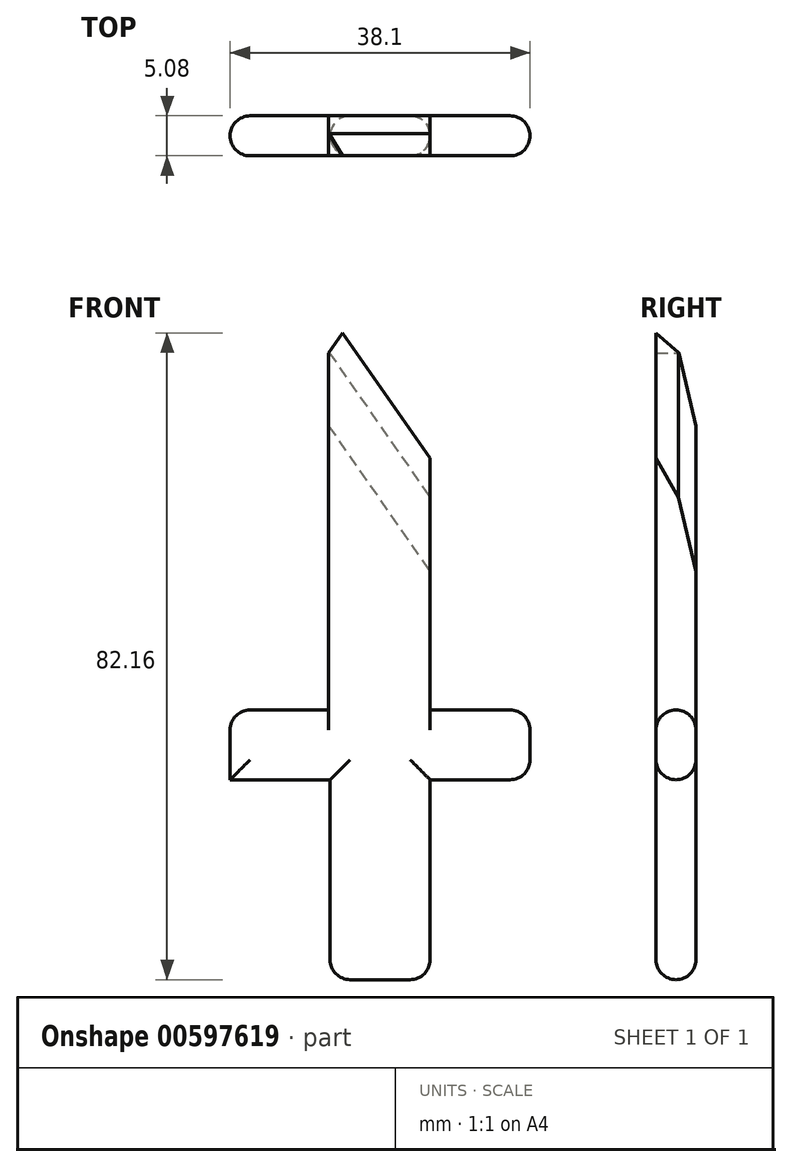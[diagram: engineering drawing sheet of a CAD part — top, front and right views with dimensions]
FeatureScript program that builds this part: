
annotation { "Feature Type Name" : "Feature", "Feature Type Description" : "" }
export const myFeature = defineFeature(function(context is Context, id is Id, definition is map)
    precondition{}
    {
        {
            var Q0;
            Q0=qCreatedBy(makeId("Front.planeOp"),FACE);
            var sketch = newSketch(context, id + "F0", { "sketchPlane" : qUnion([Q0])});
            skLineSegment(sketch, "E0.bottom", {"start": v(-30.16, 1.34) * mm, "end": v(-17.46, 1.34) * mm});
            skLineSegment(sketch, "E0.top", {"start": v(-30.16, -24.06) * mm, "end": v(-17.46, -24.06) * mm});
            skLineSegment(sketch, "E0.left", {"start": v(-30.16, 1.34) * mm, "end": v(-30.16, -24.06) * mm});
            skLineSegment(sketch, "E0.right", {"start": v(-17.46, 1.34) * mm, "end": v(-17.46, -24.06) * mm});
            skLineSegment(sketch, "E1.bottom", {"start": v(-30.16, 1.34) * mm, "end": v(-42.86, 1.34) * mm});
            skLineSegment(sketch, "E1.top", {"start": v(-30.16, 10.21) * mm, "end": v(-42.86, 10.21) * mm});
            skLineSegment(sketch, "E1.left", {"start": v(-30.16, 1.34) * mm, "end": v(-30.16, 10.21) * mm});
            skLineSegment(sketch, "E1.right", {"start": v(-42.86, 1.34) * mm, "end": v(-42.86, 10.21) * mm});
            skLineSegment(sketch, "E2.bottom", {"start": v(-17.46, 1.34) * mm, "end": v(-4.76, 1.34) * mm});
            skLineSegment(sketch, "E2.top", {"start": v(-17.46, 10.21) * mm, "end": v(-4.76, 10.21) * mm});
            skLineSegment(sketch, "E2.left", {"start": v(-17.46, 1.34) * mm, "end": v(-17.46, 10.21) * mm});
            skLineSegment(sketch, "E2.right", {"start": v(-4.76, 1.34) * mm, "end": v(-4.76, 10.21) * mm});
            skLineSegment(sketch, "E3", {"start": v(-17.46, 10.21) * mm, "end": v(-30.16, 10.21) * mm});
            skSolve(sketch);
        }
        {
            var Q0;
            Q0=qCreatedBy(makeId("Front.planeOp"),FACE);
            var sketch = newSketch(context, id + "F1", { "sketchPlane" : qUnion([Q0])});
            skLineSegment(sketch, "E4", {"start": v(-17.48, 10.21) * mm, "end": v(-17.48, 55.53) * mm});
            skLineSegment(sketch, "E5", {"start": v(-17.48, 55.53) * mm, "end": v(-23.92, 64.76) * mm});
            skLineSegment(sketch, "E6", {"start": v(-23.92, 64.76) * mm, "end": v(-30.35, 55.53) * mm});
            skLineSegment(sketch, "E7", {"start": v(-30.35, 55.53) * mm, "end": v(-30.35, 10.21) * mm});
            skLineSegment(sketch, "E8", {"start": v(-17.48, 10.21) * mm, "end": v(-30.35, 10.21) * mm});
            skSolve(sketch);
        }
        {
            var Q0;
            Q0 = qSketchRegion(id + "F0", true);
            extrude(context, id + "F2", {"entities" : qUnion([Q0]), "endBound" : BoundingType.SYMMETRIC, "depth" : 5.08 * mm, "offsetDistance" : 25.4 * mm});
        }
        {
            var Q0;
            Q0 = qSketchRegion(id + "F1", true);
            extrude(context, id + "F3", {"entities" : qUnion([Q0]), "operationType" : NewBodyOperationType.ADD, "endBound" : BoundingType.SYMMETRIC, "depth" : 5.08 * mm, "offsetDistance" : 25.4 * mm});
        }
        {
            var Q0;
            Q0=makeQuery(id+"F2.opExtrude","CAP_EDGE",EDGE,{"disambiguationData":[OSD([sQuery(id+"F0.wireOp",EDGE,"E2.bottom")])],"isStart":true});
            var Q1;
            Q1=makeQuery(id+"F2.opExtrude","CAP_EDGE",EDGE,{"disambiguationData":[OSD([sQuery(id+"F0.wireOp",EDGE,"E2.bottom")])],"isStart":false});
            var Q2;
            {var subQ0=sQuery(id+"F0.wireOp",EDGE,"E2.right");var subQ2=sQuery(id+"F0.wireOp",EDGE,"E3");var subQ3=sQuery(id+"F0.wireOp",EDGE,"E2.top");var subQ4=sQuery(id+"F0.wireOp",EDGE,"E1.top");Q2=makeQuery(id+"F3.boolean.opBoolean","SPLIT",EDGE,{"disambiguationData":[TD([makeQuery(id+"F2.opExtrude","SWEPT_FACE",FACE,{"disambiguationData":[OSD([subQ0])]})])],"derivedFrom":makeQuery(id+"F2.opExtrude","CAP_EDGE",EDGE,{"disambiguationData":[OSD([subQ4,subQ3,subQ2])],"isStart":true})});}
            var Q3;
            {var subQ0=sQuery(id+"F0.wireOp",EDGE,"E2.right");var subQ2=sQuery(id+"F0.wireOp",EDGE,"E3");var subQ3=sQuery(id+"F0.wireOp",EDGE,"E2.top");var subQ4=sQuery(id+"F0.wireOp",EDGE,"E1.top");Q3=makeQuery(id+"F3.boolean.opBoolean","SPLIT",EDGE,{"disambiguationData":[TD([makeQuery(id+"F2.opExtrude","SWEPT_FACE",FACE,{"disambiguationData":[OSD([subQ0])]})])],"derivedFrom":makeQuery(id+"F2.opExtrude","CAP_EDGE",EDGE,{"disambiguationData":[OSD([subQ4,subQ3,subQ2])],"isStart":false})});}
            var Q4;
            Q4=makeQuery(id+"F2.opExtrude","CAP_EDGE",EDGE,{"disambiguationData":[OSD([sQuery(id+"F0.wireOp",EDGE,"E2.right")])],"isStart":false});
            var Q5;
            Q5=makeQuery(id+"F2.opExtrude","CAP_EDGE",EDGE,{"disambiguationData":[OSD([sQuery(id+"F0.wireOp",EDGE,"E2.right")])],"isStart":true});
            var Q6;
            Q6=makeQuery(id+"F2.opExtrude","SWEPT_EDGE",EDGE,{"disambiguationData":[OSD([sQuery(id+"F0.wireOp",EDGE,"E2.top"),sQuery(id+"F0.wireOp",EDGE,"E2.right")])]});
            var Q7;
            Q7=makeQuery(id+"F2.opExtrude","SWEPT_EDGE",EDGE,{"disambiguationData":[OSD([sQuery(id+"F0.wireOp",EDGE,"E2.bottom"),sQuery(id+"F0.wireOp",EDGE,"E2.right")])]});
            var Q8;
            {var subQ1=sQuery(id+"F0.wireOp",EDGE,"E3");var subQ2=sQuery(id+"F0.wireOp",EDGE,"E2.top");var subQ3=sQuery(id+"F0.wireOp",EDGE,"E1.top");var subQ4=sQuery(id+"F0.wireOp",EDGE,"E1.right");Q8=makeQuery(id+"F3.boolean.opBoolean","SPLIT",EDGE,{"disambiguationData":[TD([makeQuery(id+"F2.opExtrude","SWEPT_FACE",FACE,{"disambiguationData":[OSD([subQ4])]})])],"derivedFrom":makeQuery(id+"F2.opExtrude","CAP_EDGE",EDGE,{"disambiguationData":[OSD([subQ3,subQ2,subQ1])],"isStart":false})});}
            var Q9;
            {var subQ1=sQuery(id+"F0.wireOp",EDGE,"E1.right");var subQ2=sQuery(id+"F0.wireOp",EDGE,"E3");var subQ3=sQuery(id+"F0.wireOp",EDGE,"E2.top");var subQ4=sQuery(id+"F0.wireOp",EDGE,"E1.top");Q9=makeQuery(id+"F3.boolean.opBoolean","SPLIT",EDGE,{"disambiguationData":[TD([makeQuery(id+"F2.opExtrude","SWEPT_FACE",FACE,{"disambiguationData":[OSD([subQ1])]})])],"derivedFrom":makeQuery(id+"F2.opExtrude","CAP_EDGE",EDGE,{"disambiguationData":[OSD([subQ4,subQ3,subQ2])],"isStart":true})});}
            var Q10;
            Q10=makeQuery(id+"F2.opExtrude","CAP_EDGE",EDGE,{"disambiguationData":[OSD([sQuery(id+"F0.wireOp",EDGE,"E1.bottom")])],"isStart":false});
            var Q11;
            Q11=makeQuery(id+"F2.opExtrude","CAP_EDGE",EDGE,{"disambiguationData":[OSD([sQuery(id+"F0.wireOp",EDGE,"E1.bottom")])],"isStart":true});
            var Q12;
            Q12=makeQuery(id+"F2.opExtrude","CAP_EDGE",EDGE,{"disambiguationData":[OSD([sQuery(id+"F0.wireOp",EDGE,"E1.right")])],"isStart":false});
            var Q13;
            Q13=makeQuery(id+"F2.opExtrude","CAP_EDGE",EDGE,{"disambiguationData":[OSD([sQuery(id+"F0.wireOp",EDGE,"E1.right")])],"isStart":true});
            var Q14;
            Q14=makeQuery(id+"F2.opExtrude","SWEPT_EDGE",EDGE,{"disambiguationData":[OSD([sQuery(id+"F0.wireOp",EDGE,"E1.top"),sQuery(id+"F0.wireOp",EDGE,"E1.right")])]});
            var Q15;
            Q15=makeQuery(id+"F2.opExtrude","CAP_EDGE",EDGE,{"disambiguationData":[OSD([sQuery(id+"F0.wireOp",EDGE,"E0.right")])],"isStart":true});
            var Q16;
            Q16=makeQuery(id+"F2.opExtrude","CAP_EDGE",EDGE,{"disambiguationData":[OSD([sQuery(id+"F0.wireOp",EDGE,"E0.right")])],"isStart":false});
            var Q17;
            Q17=makeQuery(id+"F2.opExtrude","CAP_EDGE",EDGE,{"disambiguationData":[OSD([sQuery(id+"F0.wireOp",EDGE,"E0.left")])],"isStart":false});
            var Q18;
            Q18=makeQuery(id+"F2.opExtrude","CAP_EDGE",EDGE,{"disambiguationData":[OSD([sQuery(id+"F0.wireOp",EDGE,"E0.left")])],"isStart":true});
            var Q19;
            Q19=makeQuery(id+"F2.opExtrude","CAP_EDGE",EDGE,{"disambiguationData":[OSD([sQuery(id+"F0.wireOp",EDGE,"E0.top")])],"isStart":false});
            var Q20;
            Q20=makeQuery(id+"F2.opExtrude","SWEPT_FACE",FACE,{"disambiguationData":[OSD([sQuery(id+"F0.wireOp",EDGE,"E0.top")])]});
            fillet(context, id + "F4", {"entities" : qUnion([Q0, Q1, Q2, Q3, Q4, Q5, Q6, Q7, Q8, Q9, Q10, Q11, Q12, Q13, Q14, Q15, Q16, Q17, Q18, Q19, Q20]), "radius" : 2.54 * mm, "tangentPropagation" : true, "allowEdgeOverflow" : false});
        }
        {
            var Q0;
            Q0=makeQuery(id+"F3.opExtrude","CAP_EDGE",EDGE,{"disambiguationData":[OSD([sQuery(id+"F1.wireOp",EDGE,"E5")])],"isStart":true});
            chamfer(context, id + "F5", {"entities" : qUnion([Q0]), "width" : 12.7 * mm, "tangentPropagation" : true});
        }
        {
            var Q0;
            {var subQ0=sQuery(id+"F1.wireOp",EDGE,"E5");Q0=makeQuery(id+"F5.opChamfer","BLEND_EDGE",EDGE,{"blendedFrom":[makeQuery(id+"F3.opExtrude","CAP_EDGE",EDGE,{"disambiguationData":[OSD([subQ0])],"isStart":true}),makeQuery(id+"F3.boolean.opBoolean","MERGE",FACE,{"derivedFrom":[makeQuery(id+"F2.opExtrude","CAP_FACE",FACE,{"disambiguationData":[OSD([sQuery(id+"F0.wireOp",EDGE,"E0.top"),sQuery(id+"F0.wireOp",EDGE,"E0.left"),sQuery(id+"F0.wireOp",EDGE,"E0.right"),sQuery(id+"F0.wireOp",EDGE,"E1.bottom"),sQuery(id+"F0.wireOp",EDGE,"E1.top"),sQuery(id+"F0.wireOp",EDGE,"E1.right"),sQuery(id+"F0.wireOp",EDGE,"E2.bottom"),sQuery(id+"F0.wireOp",EDGE,"E2.top"),sQuery(id+"F0.wireOp",EDGE,"E2.right"),sQuery(id+"F0.wireOp",EDGE,"E3")])],"isStart":true}),makeQuery(id+"F3.opExtrude","CAP_FACE",FACE,{"disambiguationData":[OSD([sQuery(id+"F1.wireOp",EDGE,"E4"),subQ0,sQuery(id+"F1.wireOp",EDGE,"E6"),sQuery(id+"F1.wireOp",EDGE,"E7"),sQuery(id+"F1.wireOp",EDGE,"E8")])],"isStart":true})]})],"blendedInto":[makeQuery(id+"F3.boolean.opBoolean","MERGE",FACE,{"derivedFrom":[makeQuery(id+"F2.opExtrude","CAP_FACE",FACE,{"disambiguationData":[OSD([sQuery(id+"F0.wireOp",EDGE,"E0.top"),sQuery(id+"F0.wireOp",EDGE,"E0.left"),sQuery(id+"F0.wireOp",EDGE,"E0.right"),sQuery(id+"F0.wireOp",EDGE,"E1.bottom"),sQuery(id+"F0.wireOp",EDGE,"E1.top"),sQuery(id+"F0.wireOp",EDGE,"E1.right"),sQuery(id+"F0.wireOp",EDGE,"E2.bottom"),sQuery(id+"F0.wireOp",EDGE,"E2.top"),sQuery(id+"F0.wireOp",EDGE,"E2.right"),sQuery(id+"F0.wireOp",EDGE,"E3")])],"isStart":true}),makeQuery(id+"F3.opExtrude","CAP_FACE",FACE,{"disambiguationData":[OSD([sQuery(id+"F1.wireOp",EDGE,"E4"),subQ0,sQuery(id+"F1.wireOp",EDGE,"E6"),sQuery(id+"F1.wireOp",EDGE,"E7"),sQuery(id+"F1.wireOp",EDGE,"E8")])],"isStart":true})]})]});}
            chamfer(context, id + "F6", {"entities" : qUnion([Q0]), "width" : 7.62 * mm, "tangentPropagation" : true});
        }
    });
